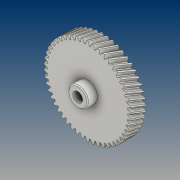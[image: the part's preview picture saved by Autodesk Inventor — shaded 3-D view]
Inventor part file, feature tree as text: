
AUTODESK INVENTOR PART (.ipt)
format: ipt  version: 2021 (Build 250183000, 183)  size: 752,640 bytes
history: native  units: mm (DEFAULTED — no unit token found)
features: extrude x4, sketch x4, plane x3, other x3, chamfer x1, pattern_circular x1, projected_geometry x1
ambient origin geometry x8: Origin, YZ Plane, XZ Plane, XY Plane, X Axis, Y Axis, Z Axis, Center Point
bodies: Solid1 (feature_tree)
feature tree (17):
  extrude  "Extrusion1"  Depth=15.0mm TaperAngle=0.0deg
  plane  "Work Plane2"
  plane  "Work Plane8"
  plane  "Work Plane9"
  other  "Spur Gear"
  sketch  "Sketch3"  dims[d16=60.0mm d17=0.0mm d34=0.628319mm]
  extrude  "Extrusion2"  Depth=10.0mm TaperAngle=0.0deg
  extrude  "Extrusion3"  Depth=0.628319mm TaperAngle=0.0deg
  chamfer  "Chamfer1"  [1 undecoded]
  extrude  "Extrusion4"  Depth=10.0mm
  pattern_circular  "Circular Pattern1"  Count=6  [1 undecoded]
  sketch  "Sketch1"  dims[d0=89.146311mm d1=15.0mm d2=0.0mm]
  sketch  "Sketch2"  dims[d3=85.134222mm d4=10.0mm d5=0.0mm]
  other  "Srf1"
  sketch  "Sketch4"  dims[d39=0.0mm d41=0.0mm d43=60.0mm d46=60.0mm d47=0.0mm d48=0.0mm d49=10.0mm d50=5.0mm d51=10.0mm d52=0.0mm d53=23.5mm d54=0.0mm d55=1.0mm d56=2.0mm d57=45.0deg d58=3.0mm d59=23.5mm d60=0.0mm d61=20.0mm d62=90.0deg]
  projected_geometry  "Projected Loop1"
  other  "Pitch Diameter"
note: 2 required parameter values undecoded (feature->parameter linkage not recoverable at this tier; creation-order binding heuristic only, values carry confidence <= 0.55)
